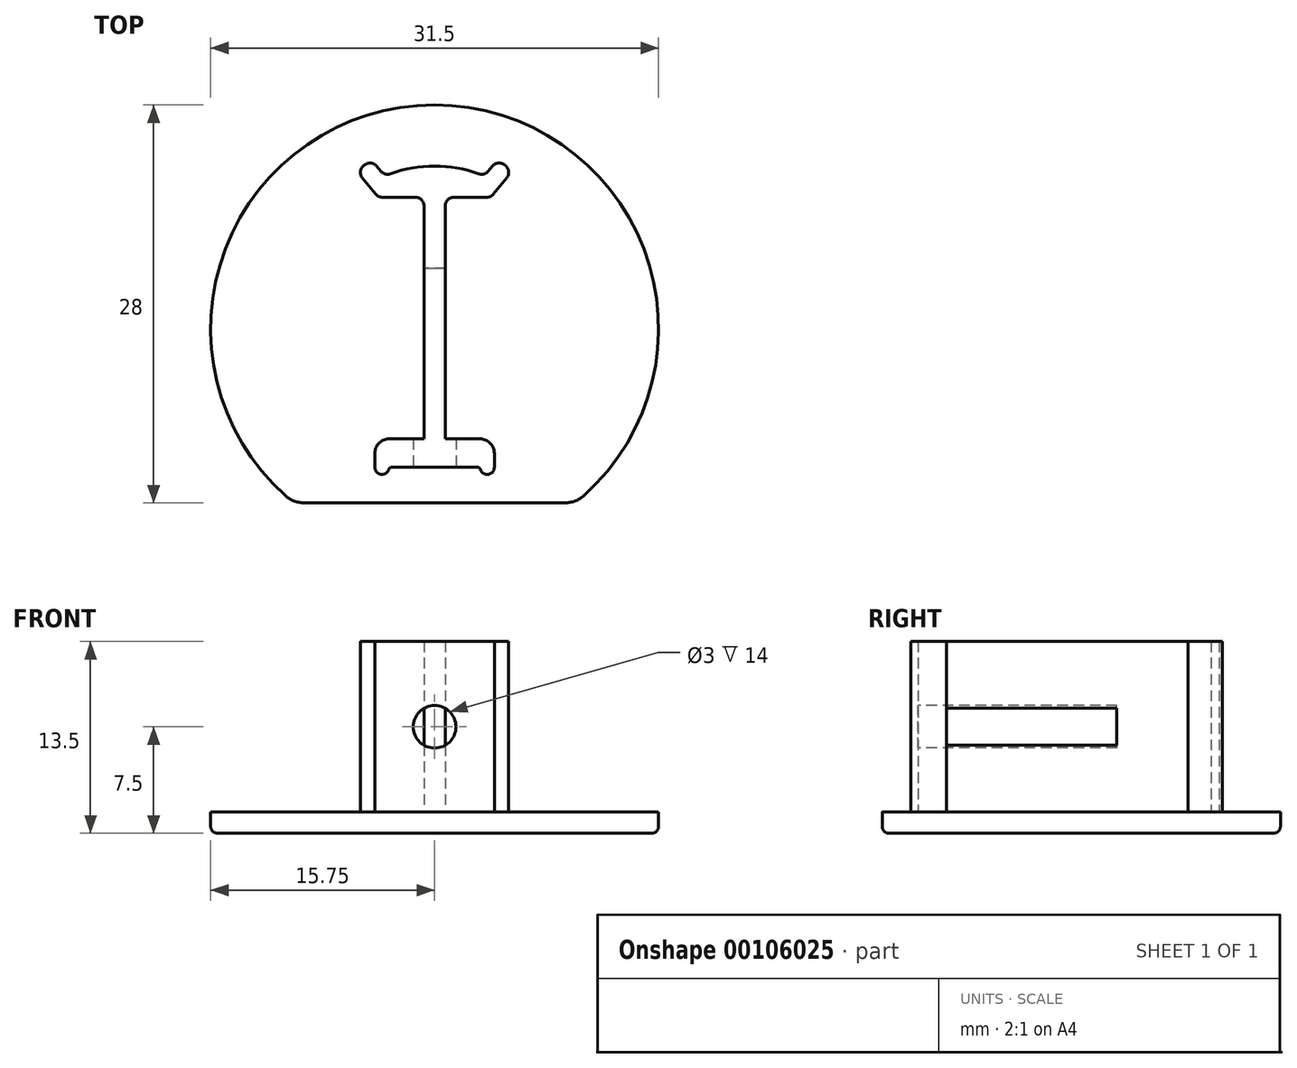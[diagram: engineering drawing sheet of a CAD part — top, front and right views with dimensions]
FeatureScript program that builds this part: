
annotation { "Feature Type Name" : "Feature", "Feature Type Description" : "" }
export const myFeature = defineFeature(function(context is Context, id is Id, definition is map)
    precondition{}
    {
        {
            var Q0;
            Q0=qCreatedBy(makeId("Top.planeOp"),FACE);
            var sketch = newSketch(context, id + "F0", { "sketchPlane" : qUnion([Q0])});
            skCircle(sketch, "E0", {"center": v(0, 0) * mm, "radius": 15.75 * mm});
            skLineSegment(sketch, "E1", {"start": v(-9.9, -12.25) * mm, "end": v(9.9, -12.25) * mm});
            skSolve(sketch);
        }
        {
            var Q0;
            {var subQ0=sQuery(id+"F0.wireOp",EDGE,"E1");Q0=makeQuery(id+"F0.imprint","IMPRINT",FACE,{"disambiguationData":[TD([[makeQuery(id+"F0.imprint","IMPRINT",EDGE,{"derivedFrom":subQ0}),1.0]])]});}
            extrude(context, id + "F1", {"entities" : qUnion([Q0]), "depth" : 1.5 * mm});
        }
        {
            var Q0;
            Q0=makeQuery(id+"F1.opExtrude","CAP_FACE",FACE,{"disambiguationData":[OSD([sQuery(id+"F0.wireOp",EDGE,"E0"),sQuery(id+"F0.wireOp",EDGE,"E1")])],"isStart":false});
            var sketch = newSketch(context, id + "F2", { "sketchPlane" : qUnion([Q0])});
            skLineSegment(sketch, "E2", {"start": v(0, 11.45) * mm, "end": v(0, -9.75) * mm, "construction": true});
            skLineSegment(sketch, "E3", {"start": v(0, -9.75) * mm, "end": v(-3.03, -9.75) * mm});
            skLineSegment(sketch, "E4", {"start": v(-4.2, -9.75) * mm, "end": v(-4.2, -8.75) * mm});
            skLineSegment(sketch, "E5", {"start": v(-3.2, -7.75) * mm, "end": v(-0.75, -7.75) * mm});
            skLineSegment(sketch, "E6", {"start": v(-0.75, -7.75) * mm, "end": v(-0.75, 8.65) * mm});
            skLineSegment(sketch, "E7", {"start": v(-1.35, 9.25) * mm, "end": v(-3.67, 9.25) * mm});
            skLineSegment(sketch, "E8", {"start": v(-4.13, 9.47) * mm, "end": v(-5.08, 10.62) * mm});
            skArc(sketch, "E9", {"start": v(0, 11.45) * mm, "mid": v(-1.58, 11.31) * mm, "end": v(-3.1, 10.9) * mm});
            skLineSegment(sketch, "E10", {"start": v(0, 11.45) * mm, "end": v(1.43, 11.45) * mm, "construction": true});
            skLineSegment(sketch, "E11", {"start": v(-3.78, 11.09) * mm, "end": v(-4.07, 11.45) * mm});
            skLineSegment(sketch, "E12", {"start": v(-4.92, 11.53) * mm, "end": v(-5, 11.46) * mm});
            skPoint(sketch, "E13.visualSharp", {"position": v(-0.75, -7.75) * mm});
            skPoint(sketch, "E14.visualSharp", {"position": v(-5.46, 11.08) * mm});
            skArc(sketch, "E14.filletArc", {"start": v(-5, 11.46) * mm, "mid": v(-5.2, 11.06) * mm, "end": v(-5.08, 10.62) * mm});
            skPoint(sketch, "E15.visualSharp", {"position": v(-4.45, 11.9) * mm});
            skArc(sketch, "E15.filletArc", {"start": v(-4.07, 11.45) * mm, "mid": v(-4.48, 11.66) * mm, "end": v(-4.92, 11.53) * mm});
            skPoint(sketch, "E16.visualSharp", {"position": v(-3.95, 9.25) * mm});
            skArc(sketch, "E16.filletArc", {"start": v(-4.13, 9.47) * mm, "mid": v(-3.92, 9.3) * mm, "end": v(-3.67, 9.25) * mm});
            skPoint(sketch, "E17.visualSharp", {"position": v(-3.5, 10.75) * mm});
            skArc(sketch, "E17.filletArc", {"start": v(-3.78, 11.09) * mm, "mid": v(-3.47, 10.89) * mm, "end": v(-3.1, 10.9) * mm});
            skPoint(sketch, "E18.visualSharp", {"position": v(-0.75, 9.25) * mm});
            skArc(sketch, "E18.filletArc", {"start": v(-0.75, 8.65) * mm, "mid": v(-0.93, 9.07) * mm, "end": v(-1.35, 9.25) * mm});
            skPoint(sketch, "E19.visualSharp", {"position": v(-4.2, -7.75) * mm});
            skArc(sketch, "E19.filletArc", {"start": v(-3.2, -7.75) * mm, "mid": v(-3.9, -8.04) * mm, "end": v(-4.2, -8.75) * mm});
            skArc(sketch, "E20", {"start": v(-4.2, -9.75) * mm, "mid": v(-3.77, -10.24) * mm, "end": v(-3.22, -9.9) * mm});
            skPoint(sketch, "E21.visualSharp", {"position": v(-3.2, -9.75) * mm});
            skArc(sketch, "E21.filletArc", {"start": v(-3.03, -9.75) * mm, "mid": v(-3.15, -9.79) * mm, "end": v(-3.22, -9.9) * mm});
            skArc(sketch, "E22.MirrorCS", {"start": v(4.07, 11.45) * mm, "mid": v(4.48, 11.66) * mm, "end": v(4.92, 11.53) * mm});
            skArc(sketch, "E23.MirrorCS", {"start": v(3.03, -9.75) * mm, "mid": v(3.15, -9.79) * mm, "end": v(3.22, -9.9) * mm});
            skArc(sketch, "E24.MirrorCS", {"start": v(4.13, 9.47) * mm, "mid": v(3.92, 9.3) * mm, "end": v(3.67, 9.25) * mm});
            skLineSegment(sketch, "E25.MirrorCS", {"start": v(4.92, 11.53) * mm, "end": v(5, 11.46) * mm});
            skLineSegment(sketch, "E26.MirrorCS", {"start": v(3.78, 11.09) * mm, "end": v(4.07, 11.45) * mm});
            skArc(sketch, "E27.MirrorCS", {"start": v(5, 11.46) * mm, "mid": v(5.2, 11.06) * mm, "end": v(5.08, 10.62) * mm});
            skLineSegment(sketch, "E28.MirrorCS", {"start": v(4.2, -9.75) * mm, "end": v(4.2, -8.75) * mm});
            skArc(sketch, "E29.MirrorCS", {"start": v(3.78, 11.09) * mm, "mid": v(3.47, 10.89) * mm, "end": v(3.1, 10.9) * mm});
            skArc(sketch, "E30.MirrorCS", {"start": v(0.75, 8.65) * mm, "mid": v(0.93, 9.07) * mm, "end": v(1.35, 9.25) * mm});
            skArc(sketch, "E31.MirrorCS", {"start": v(3.2, -7.75) * mm, "mid": v(3.9, -8.04) * mm, "end": v(4.2, -8.75) * mm});
            skArc(sketch, "E32.MirrorCS", {"start": v(4.2, -9.75) * mm, "mid": v(3.77, -10.24) * mm, "end": v(3.22, -9.9) * mm});
            skArc(sketch, "E33.MirrorCS", {"start": v(0, 11.45) * mm, "mid": v(1.58, 11.31) * mm, "end": v(3.1, 10.9) * mm});
            skLineSegment(sketch, "E34.MirrorCS", {"start": v(0, 11.45) * mm, "end": v(-1.43, 11.45) * mm, "construction": true});
            skLineSegment(sketch, "E35.MirrorCS", {"start": v(4.13, 9.47) * mm, "end": v(5.08, 10.62) * mm});
            skLineSegment(sketch, "E36.MirrorCS", {"start": v(1.35, 9.25) * mm, "end": v(3.67, 9.25) * mm});
            skLineSegment(sketch, "E37.MirrorCS", {"start": v(0.75, -7.75) * mm, "end": v(0.75, 8.65) * mm});
            skLineSegment(sketch, "E38.MirrorCS", {"start": v(3.2, -7.75) * mm, "end": v(0.75, -7.75) * mm});
            skLineSegment(sketch, "E39.MirrorCS", {"start": v(0, -9.75) * mm, "end": v(3.03, -9.75) * mm});
            skPoint(sketch, "E40.MirrorP", {"position": v(0.75, 9.25) * mm});
            skPoint(sketch, "E41.MirrorP", {"position": v(4.2, -7.75) * mm});
            skPoint(sketch, "E42.MirrorP", {"position": v(5.46, 11.08) * mm});
            skPoint(sketch, "E43.MirrorP", {"position": v(0.75, -7.75) * mm});
            skPoint(sketch, "E44.MirrorP", {"position": v(3.5, 10.75) * mm});
            skPoint(sketch, "E45.MirrorP", {"position": v(3.2, -9.75) * mm});
            skPoint(sketch, "E46.MirrorP", {"position": v(4.45, 11.9) * mm});
            skPoint(sketch, "E47.MirrorP", {"position": v(3.95, 9.25) * mm});
            skSolve(sketch);
        }
        {
            var Q0;
            Q0=makeQuery(id+"F2.imprint","IMPRINT",FACE,{"disambiguationData":[TD([[makeQuery(id+"F2.imprint","IMPRINT",EDGE,{"derivedFrom":sQuery(id+"F2.wireOp",EDGE,"E3")}),-1.0]])]});
            extrude(context, id + "F3", {"entities" : qUnion([Q0]), "operationType" : NewBodyOperationType.ADD, "depth" : 12 * mm});
        }
        {
            var Q0;
            Q0=makeQuery(id+"F1.opExtrude","CAP_EDGE",EDGE,{"disambiguationData":[OSD([sQuery(id+"F0.wireOp",EDGE,"E0")])],"isStart":true});
            var Q1;
            Q1=makeQuery(id+"F1.opExtrude","CAP_EDGE",EDGE,{"disambiguationData":[OSD([sQuery(id+"F0.wireOp",EDGE,"E1")])],"isStart":true});
            fillet(context, id + "F4", {"entities" : qUnion([Q0, Q1]), "radius" : .5 * mm, "tangentPropagation" : true, "allowEdgeOverflow" : false});
        }
        {
            var Q0;
            {var subQ0=sQuery(id+"F0.wireOp",EDGE,"E1");var subQ1=sQuery(id+"F0.wireOp",EDGE,"E0");Q0=makeQuery(id+"F1.opExtrude","SWEPT_EDGE",EDGE,{"disambiguationData":[OSD([subQ1,subQ0]),TDD([makeQuery(id+"F0.imprint","INTERSECT",VERTEX,{"disambiguationData":[OD(1.0)],"derivedFrom":[subQ1,subQ0]})])]});}
            var Q1;
            {var subQ0=sQuery(id+"F0.wireOp",EDGE,"E1");var subQ1=sQuery(id+"F0.wireOp",EDGE,"E0");Q1=makeQuery(id+"F1.opExtrude","SWEPT_EDGE",EDGE,{"disambiguationData":[OSD([subQ1,subQ0]),TDD([makeQuery(id+"F0.imprint","INTERSECT",VERTEX,{"disambiguationData":[OD(0.0)],"derivedFrom":[subQ1,subQ0]})])]});}
            fillet(context, id + "F5", {"entities" : qUnion([Q0, Q1]), "radius" : 2 * mm, "tangentPropagation" : true, "allowEdgeOverflow" : false});
        }
        {
            var Q0;
            Q0=makeQuery(id+"F3.opExtrude","SWEPT_FACE",FACE,{"disambiguationData":[OSD([sQuery(id+"F2.wireOp",EDGE,"E3"),sQuery(id+"F2.wireOp",EDGE,"E39.MirrorCS")])]});
            var sketch = newSketch(context, id + "F6", { "sketchPlane" : qUnion([Q0])});
            skCircle(sketch, "E48", {"center": v(0, 7.5) * mm, "radius": 1.5 * mm});
            skSolve(sketch);
        }
        {
            var Q0;
            Q0=makeQuery(id+"F6.imprint","IMPRINT",FACE,{"disambiguationData":[TD([[makeQuery(id+"F6.imprint","IMPRINT",EDGE,{"derivedFrom":sQuery(id+"F6.wireOp",EDGE,"E48")}),1.0]])]});
            extrude(context, id + "F7", {"entities" : qUnion([Q0]), "operationType" : NewBodyOperationType.REMOVE, "oppositeDirection" : true, "depth" : 14 * mm});
        }
    });
